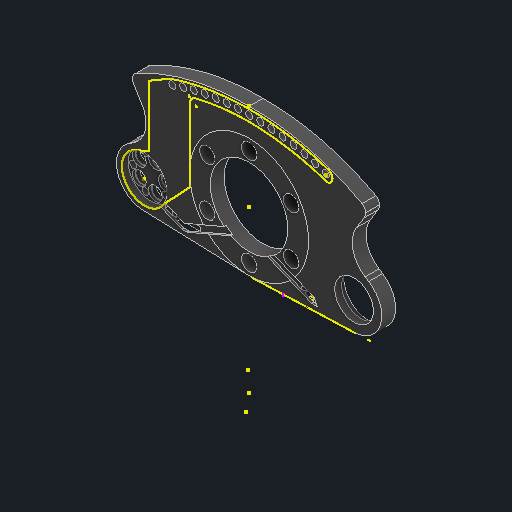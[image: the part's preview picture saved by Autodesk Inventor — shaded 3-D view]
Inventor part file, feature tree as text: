
AUTODESK INVENTOR PART (.ipt)
format: ipt  version: 2022 (Build 260153000, 153)  size: 582,144 bytes
history: native  units: mm
features: sketch x8, other x3
ambient origin geometry x8: Origin, YZ Plane, XZ Plane, XY Plane, X Axis, Y Axis, Z Axis, Center Point
bodies: Solid1 (feature_tree)
feature tree (11):
  other  "buttonMount-v2.ipt"
  other  "Solid1::buttonMount-v2.ipt"
  other  "TaggingFeature1"
  sketch  "Sketch1"  dims[d0=10.0mm]
  sketch  "Sketch2"
  sketch  "Sketch4"
  sketch  "Sketch5"
  sketch  "Sketch7"
  sketch  "Sketch8"
  sketch  "Sketch11"
  sketch  "Sketch12"
